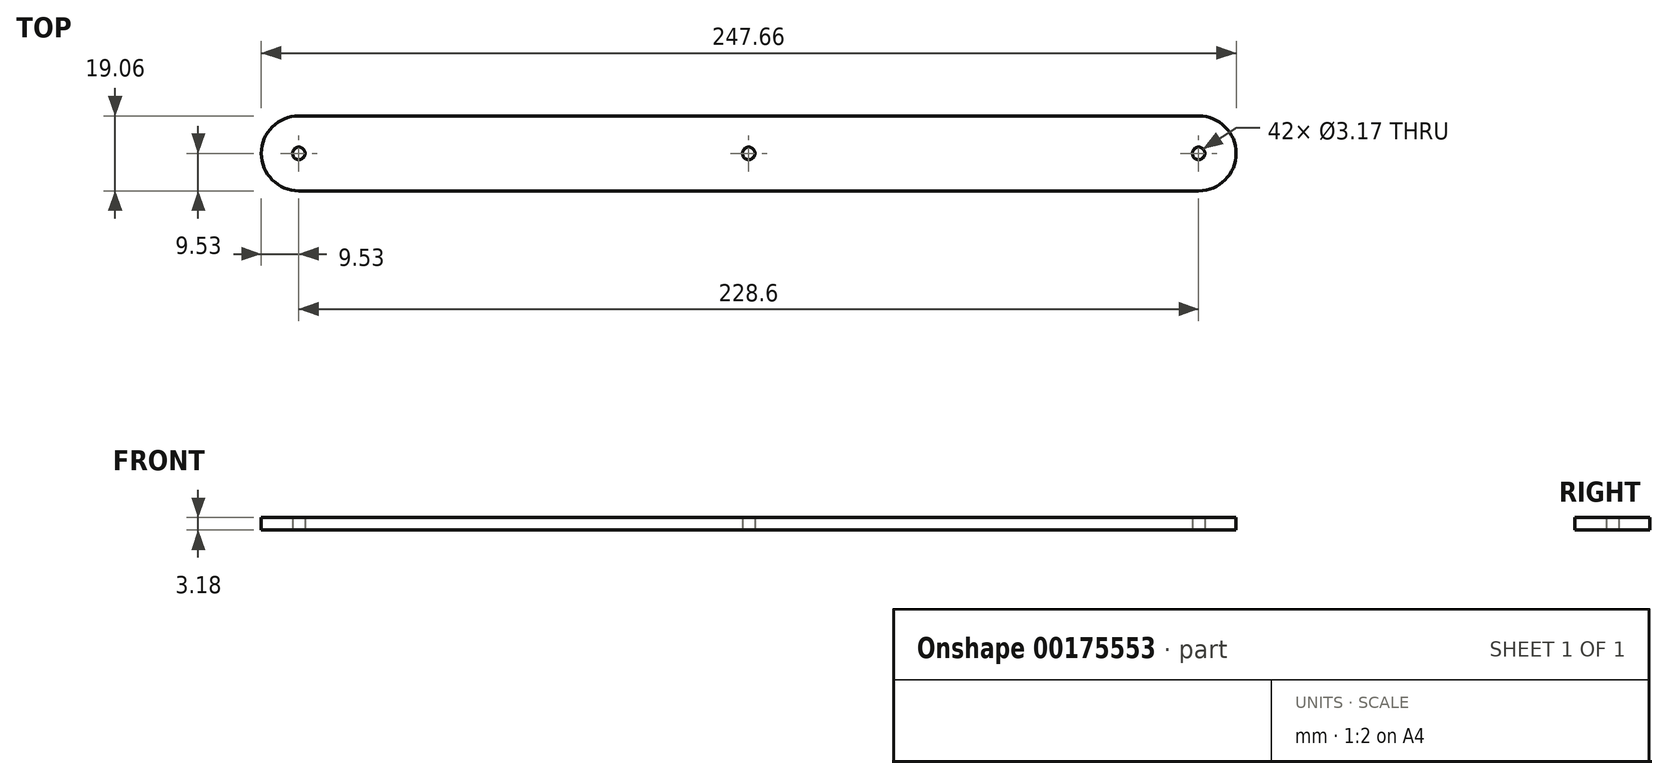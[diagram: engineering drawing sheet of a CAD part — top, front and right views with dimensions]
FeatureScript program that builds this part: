
annotation { "Feature Type Name" : "Feature", "Feature Type Description" : "" }
export const myFeature = defineFeature(function(context is Context, id is Id, definition is map)
    precondition{}
    {
        {
            var Q0;
            Q0=qCreatedBy(makeId("Top.planeOp"),FACE);
            var sketch = newSketch(context, id + "F0", { "sketchPlane" : qUnion([Q0])});
            skLineSegment(sketch, "E0.bottom", {"start": v(114.3, 9.53) * mm, "end": v(-114.3, 9.53) * mm});
            skLineSegment(sketch, "E0.top", {"start": v(114.3, -9.53) * mm, "end": v(-114.3, -9.53) * mm});
            skPoint(sketch, "E0.middle", {"position": v(0, 0) * mm});
            skArc(sketch, "E1", {"start": v(-114.3, 9.53) * mm, "mid": v(-123.83, 0) * mm, "end": v(-114.3, -9.53) * mm});
            skArc(sketch, "E2", {"start": v(114.3, -9.53) * mm, "mid": v(123.83, 0) * mm, "end": v(114.3, 9.53) * mm});
            skCircle(sketch, "E3", {"center": v(-114.3, 0) * mm, "radius": 1.59 * mm});
            skCircle(sketch, "E4", {"center": v(114.3, 0) * mm, "radius": 1.59 * mm});
            skCircle(sketch, "E5", {"center": v(0, 0) * mm, "radius": 1.59 * mm});
            skSolve(sketch);
        }
        {
            var Q0;
            Q0 = qSketchRegion(id + "F0", true);
            extrude(context, id + "F1", {"entities" : qUnion([Q0]), "depth" : 3.17 * mm});
        }
    });
